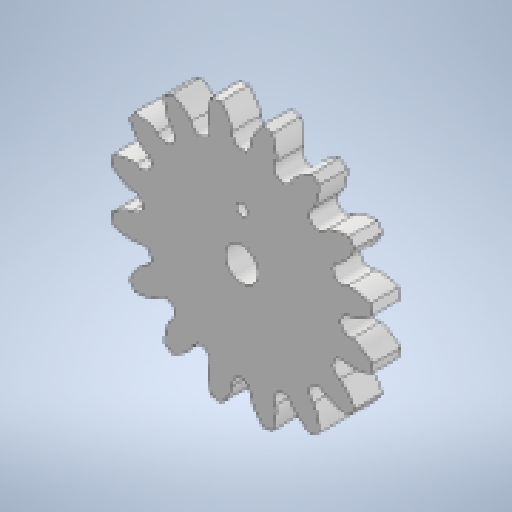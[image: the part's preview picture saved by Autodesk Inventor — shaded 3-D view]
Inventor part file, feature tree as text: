
AUTODESK INVENTOR PART (.ipt)
format: ipt  version: 2025 (Build 290162010, 162A)  size: 323,584 bytes
history: native  units: mm
features: extrude x4, sketch x3, pattern_circular x2
ambient origin geometry x8: Origin, YZ Plane, XZ Plane, XY Plane, X Axis, Y Axis, Z Axis, Center Point
bodies: Solid1 (feature_tree)
feature tree (9):
  extrude  "Extrusion1"  TaperAngle=0.0deg  [1 undecoded]
  extrude  "Extrusion2"  Depth=28.0mm
  pattern_circular  "Circular Pattern1"  Count=8  [1 undecoded]
  extrude  "Extrusion3"  Depth=10.0mm TaperAngle=0.0deg
  extrude  "Extrusion4"  Depth=10.0mm TaperAngle=360.0deg
  pattern_circular  "Circular Pattern2"  [2 undecoded]
  sketch  "Sketch2"  dims[d0=24.0mm d1=0.0mm d2=0.0mm d3=0.0mm]
  sketch  "Sketch Circular Pattern2"  dims[d4=160.0mm d5=360.0deg d7=28.0mm d8=80.0mm]
  sketch  "Sketch3"  dims[d10=8.0mm d15=10.0mm d16=0.0mm d17=80.0mm d19=360.0deg d21=125.0mm d22=22.5deg d23=22.5deg d24=15.0mm d25=0.0mm d26=0.0mm d27=40.0mm d28=360.0deg]
note: 4 required parameter values undecoded (feature->parameter linkage not recoverable at this tier; creation-order binding heuristic only, values carry confidence <= 0.55)
